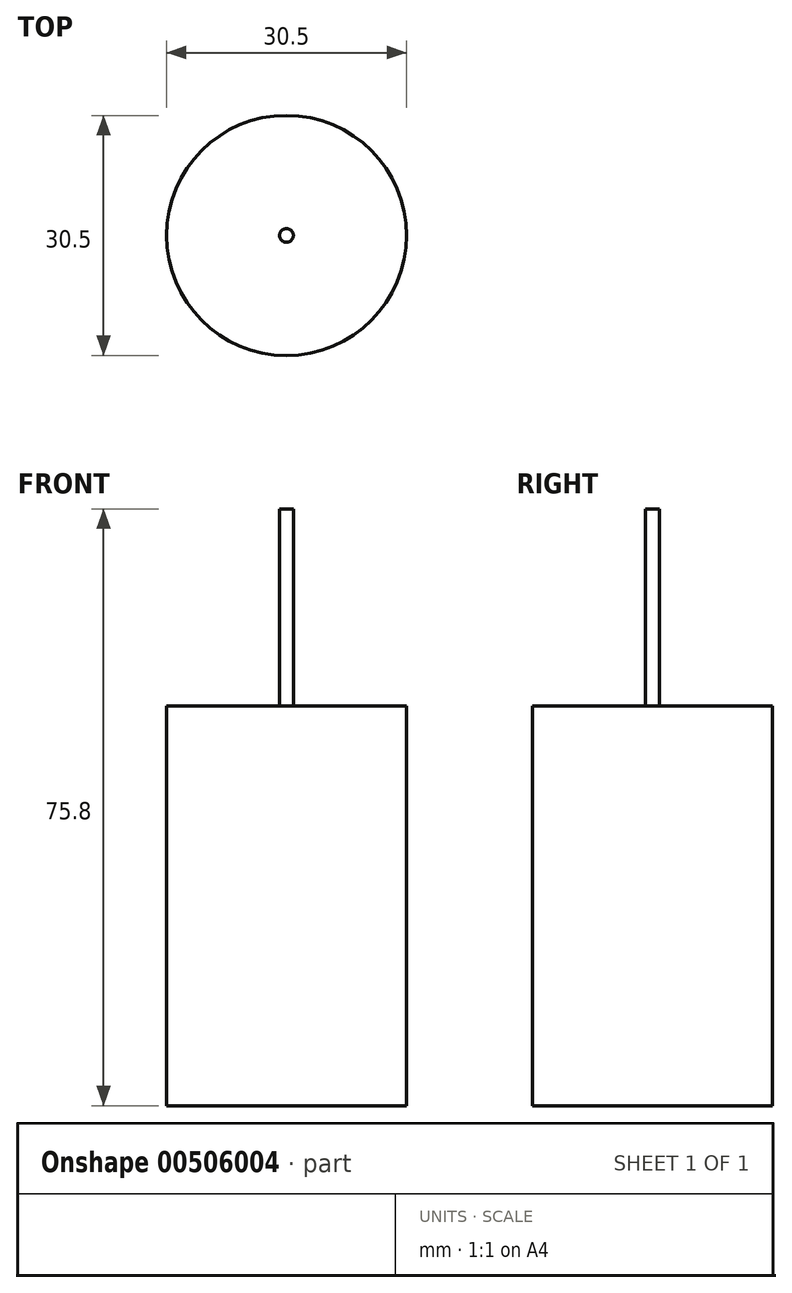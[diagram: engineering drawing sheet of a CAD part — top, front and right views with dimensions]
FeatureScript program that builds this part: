
annotation { "Feature Type Name" : "Feature", "Feature Type Description" : "" }
export const myFeature = defineFeature(function(context is Context, id is Id, definition is map)
    precondition{}
    {
        {
            var Q0;
            Q0=qCreatedBy(makeId("Top.planeOp"),FACE);
            var sketch = newSketch(context, id + "F0", { "sketchPlane" : qUnion([Q0])});
            skCircle(sketch, "E0", {"center": v(0, 0) * mm, "radius": 15.25 * mm});
            skSolve(sketch);
        }
        {
            var Q0;
            Q0 = qSketchRegion(id + "F0", true);
            var Q1;
            Q1=makeQuery(id+"F0.imprint","IMPRINT",FACE,{"disambiguationData":[TD([[makeQuery(id+"F0.imprint","IMPRINT",EDGE,{"derivedFrom":sQuery(id+"F0.wireOp",EDGE,"E0")}),1.0]])]});
            extrude(context, id + "F1", {"entities" : qUnion([Q0, Q1]), "depth" : 50.8 * mm, "offsetDistance" : 25 * mm});
        }
        {
            var Q0;
            Q0=makeQuery(id+"F1.opExtrude","CAP_FACE",FACE,{"disambiguationData":[OSD([sQuery(id+"F0.wireOp",EDGE,"E0")])],"isStart":false});
            var sketch = newSketch(context, id + "F2", { "sketchPlane" : qUnion([Q0])});
            skCircle(sketch, "E1", {"center": v(0, 0) * mm, "radius": 0.87 * mm});
            skSolve(sketch);
        }
        {
            var Q0;
            Q0 = qSketchRegion(id + "F2", true);
            extrude(context, id + "F3", {"entities" : qUnion([Q0]), "operationType" : NewBodyOperationType.ADD, "depth" : 25 * mm, "offsetDistance" : 25 * mm});
        }
    });
